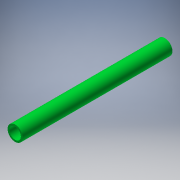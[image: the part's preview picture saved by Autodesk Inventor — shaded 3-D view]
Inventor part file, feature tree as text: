
AUTODESK INVENTOR PART (.ipt)
format: ipt  version: 2018.2 (Build 222227000, 227)  size: 107,520 bytes
history: native  units: in
note: dims shown in document units (in); Inventor stores cm internally (conversion verified against a paired STEP export)
features: extrude x1, sketch x1
ambient origin geometry x8: Origin, YZ Plane, XZ Plane, XY Plane, X Axis, Y Axis, Z Axis, Center Point
bodies: Solid1 (feature_tree)
feature tree (2):
  extrude  "Extrusion1"  Depth=13.0in
  sketch  "Sketch1"  dims[d0=1.315in d1=1.0in d2=13.0in d3=0.0in]
